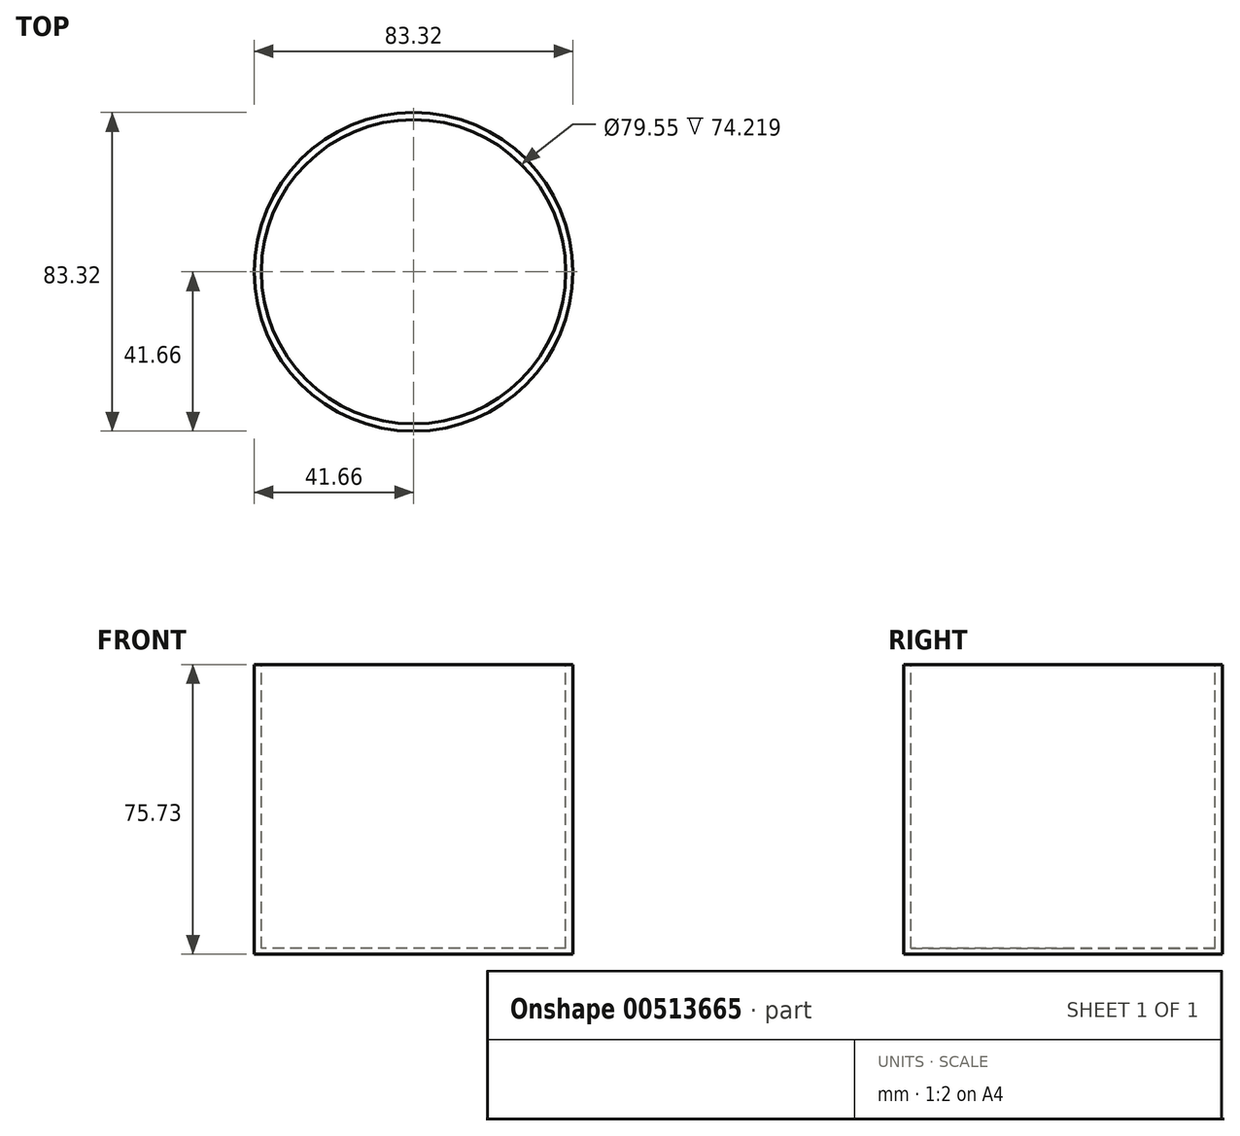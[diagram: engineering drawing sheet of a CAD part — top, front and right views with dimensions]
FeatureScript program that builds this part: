
annotation { "Feature Type Name" : "Feature", "Feature Type Description" : "" }
export const myFeature = defineFeature(function(context is Context, id is Id, definition is map)
    precondition{}
    {
        {
            var Q0;
            Q0=qCreatedBy(makeId("Front.planeOp"),FACE);
            var sketch = newSketch(context, id + "F0", { "sketchPlane" : qUnion([Q0])});
            skLineSegment(sketch, "E0", {"start": v(0, -61.53) * mm, "end": v(29.6, -61.53) * mm});
            skLineSegment(sketch, "E1", {"start": v(29.6, -61.53) * mm, "end": v(41.66, -61.53) * mm});
            skLineSegment(sketch, "E2", {"start": v(41.66, -61.53) * mm, "end": v(41.66, 14.2) * mm});
            skLineSegment(sketch, "E3", {"start": v(41.66, 14.2) * mm, "end": v(39.77, 14.2) * mm, "construction": true});
            skLineSegment(sketch, "E4", {"start": v(39.77, 14.2) * mm, "end": v(39.77, -60.02) * mm});
            skLineSegment(sketch, "E5", {"start": v(39.77, -60.02) * mm, "end": v(0, -60.02) * mm});
            skLineSegment(sketch, "E6", {"start": v(39.77, 14.2) * mm, "end": v(41.66, 14.2) * mm});
            skLineSegment(sketch, "E7", {"start": v(0, 75.6) * mm, "end": v(0, -76.4) * mm, "construction": true});
            skLineSegment(sketch, "E8", {"start": v(0, -60.02) * mm, "end": v(0, -60.7) * mm});
            skLineSegment(sketch, "E9", {"start": v(0, -61.53) * mm, "end": v(0, -60.02) * mm});
            skSolve(sketch);
        }
        {
            var Q0;
            {var subQ0=sQuery(id+"F0.wireOp",EDGE,"E0");Q0=makeQuery(id+"F0.imprint","IMPRINT",FACE,{"disambiguationData":[TD([[makeQuery(id+"F0.imprint","IMPRINT",EDGE,{"derivedFrom":subQ0}),1.0]])]});}
            var Q1;
            Q1=sQuery(id+"F0.wireOp",EDGE,"E7");
            revolve(context, id + "F1", {"entities" : qUnion([Q0]), "axis" : qUnion([Q1]), "revolveType" : RevolveType.FULL});
        }
    });
